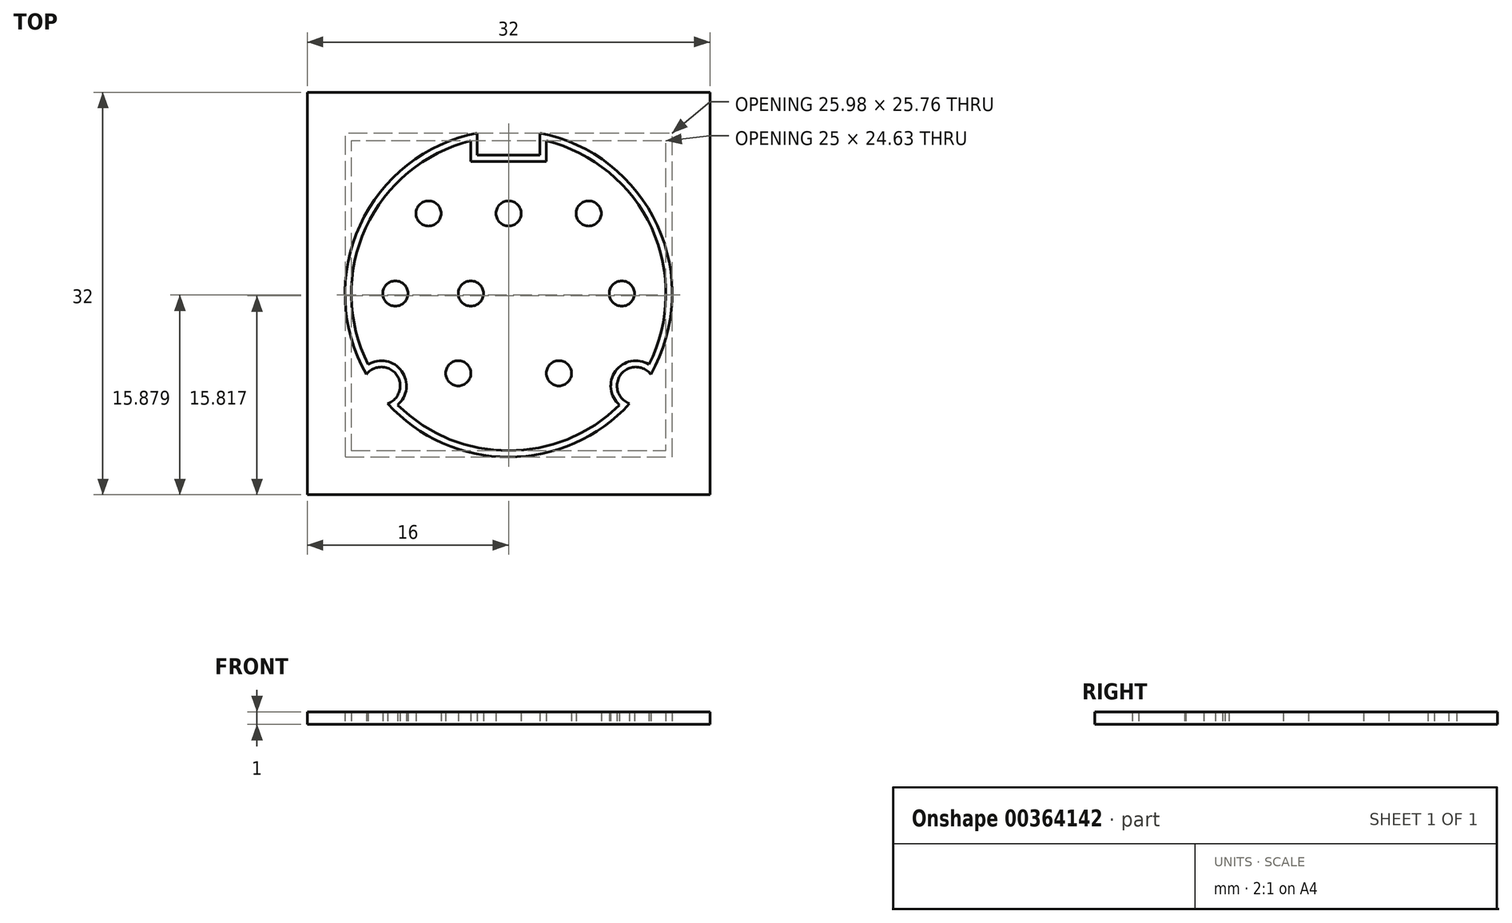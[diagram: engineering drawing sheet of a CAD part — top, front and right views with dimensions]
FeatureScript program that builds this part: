
annotation { "Feature Type Name" : "Feature", "Feature Type Description" : "" }
export const myFeature = defineFeature(function(context is Context, id is Id, definition is map)
    precondition{}
    {
        {
            var Q0;
            Q0=qCreatedBy(makeId("Top.planeOp"),FACE);
            var sketch = newSketch(context, id + "F0", { "sketchPlane" : qUnion([Q0])});
            skArc(sketch, "E0", {"start": v(-12.05, -3.32) * mm, "mid": v(-11.66, -4.5) * mm, "end": v(-11.16, -5.63) * mm});
            skCircle(sketch, "E1", {"center": v(0, 6.36) * mm, "radius": 1 * mm});
            skCircle(sketch, "E2", {"center": v(-9, 0) * mm, "radius": 1 * mm});
            skCircle(sketch, "E3", {"center": v(9, 0) * mm, "radius": 1 * mm});
            skCircle(sketch, "E4", {"center": v(-6.36, 6.36) * mm, "radius": 1 * mm});
            skCircle(sketch, "E5", {"center": v(6.36, 6.36) * mm, "radius": 1 * mm});
            skArc(sketch, "E6", {"start": v(1.5, -12.91) * mm, "mid": v(5.93, -11.57) * mm, "end": v(9.61, -8.75) * mm});
            skLineSegment(sketch, "E7.bottom", {"start": v(16, 16) * mm, "end": v(-16, 16) * mm});
            skLineSegment(sketch, "E7.top", {"start": v(16, -16) * mm, "end": v(-16, -16) * mm});
            skLineSegment(sketch, "E7.left", {"start": v(16, 16) * mm, "end": v(16, -16) * mm});
            skLineSegment(sketch, "E7.right", {"start": v(-16, 16) * mm, "end": v(-16, -16) * mm});
            skArc(sketch, "E8", {"start": v(-3, 12.13) * mm, "mid": v(-11.36, 5.22) * mm, "end": v(-11.16, -5.63) * mm});
            skArc(sketch, "E9", {"start": v(-2.5, 12.76) * mm, "mid": v(-11.81, 5.42) * mm, "end": v(-11.3, -6.42) * mm});
            skCircle(sketch, "E10", {"center": v(-3, 0) * mm, "radius": 1 * mm});
            skCircle(sketch, "E11", {"center": v(-4, -6.34) * mm, "radius": 1 * mm});
            skCircle(sketch, "E12", {"center": v(4, -6.34) * mm, "radius": 1 * mm});
            skLineSegment(sketch, "E13.bottom", {"start": v(2.5, 11) * mm, "end": v(-2.5, 11) * mm});
            skLineSegment(sketch, "E13.left", {"start": v(2.5, 11) * mm, "end": v(2.5, 12.76) * mm});
            skLineSegment(sketch, "E13.right", {"start": v(-2.5, 11) * mm, "end": v(-2.5, 12.76) * mm});
            skLineSegment(sketch, "E14.bottom", {"start": v(3, 10.5) * mm, "end": v(-3, 10.5) * mm});
            skLineSegment(sketch, "E14.left", {"start": v(3, 10.5) * mm, "end": v(3, 12.13) * mm});
            skLineSegment(sketch, "E14.right", {"start": v(-3, 10.5) * mm, "end": v(-3, 12.13) * mm});
            skArc(sketch, "E15", {"start": v(-8.82, -8.86) * mm, "mid": v(-8.5, -6.17) * mm, "end": v(-11.16, -5.63) * mm});
            skArc(sketch, "E16", {"start": v(-9.61, -8.75) * mm, "mid": v(-8.9, -6.46) * mm, "end": v(-11.3, -6.42) * mm});
            skArc(sketch, "E17", {"start": v(11.16, -5.63) * mm, "mid": v(8.5, -6.17) * mm, "end": v(8.82, -8.86) * mm});
            skArc(sketch, "E18", {"start": v(11.3, -6.42) * mm, "mid": v(8.9, -6.46) * mm, "end": v(9.61, -8.75) * mm});
            skArc(sketch, "E19.trimOffspring", {"start": v(-8.82, -8.86) * mm, "mid": v(0, -12.5) * mm, "end": v(8.82, -8.86) * mm});
            skPoint(sketch, "E20.start.orphan", {"position": v(-4, -7.34) * mm});
            skPoint(sketch, "E21.orphan", {"position": v(4, -7.34) * mm});
            skArc(sketch, "E22.trimOffspring", {"start": v(11.16, -5.63) * mm, "mid": v(11.36, 5.22) * mm, "end": v(3, 12.13) * mm});
            skArc(sketch, "E23.trimOffspring", {"start": v(11.16, -5.63) * mm, "mid": v(11.66, -4.5) * mm, "end": v(12.05, -3.32) * mm});
            skArc(sketch, "E24.trimOffspring", {"start": v(-9.61, -8.75) * mm, "mid": v(-5.93, -11.57) * mm, "end": v(-1.5, -12.91) * mm});
            skArc(sketch, "E25.trimOffspring", {"start": v(-9.61, -8.75) * mm, "mid": v(0, -13) * mm, "end": v(9.61, -8.75) * mm});
            skArc(sketch, "E26.trimOffspring", {"start": v(11.3, -6.42) * mm, "mid": v(11.81, 5.42) * mm, "end": v(2.5, 12.76) * mm});
            skSolve(sketch);
        }
        {
            var Q0;
            Q0=makeQuery(id+"F0.imprint","IMPRINT",FACE,{"disambiguationData":[TD([[makeQuery(id+"F0.imprint","IMPRINT",EDGE,{"derivedFrom":sQuery(id+"F0.wireOp",EDGE,"E13.bottom")}),1.0]])]});
            var Q1;
            Q1=makeQuery(id+"F0.imprint","IMPRINT",FACE,{"disambiguationData":[TD([[makeQuery(id+"F0.imprint","IMPRINT",EDGE,{"derivedFrom":sQuery(id+"F0.wireOp",EDGE,"E2")}),1.0]])]});
            var Q2;
            Q2=makeQuery(id+"F0.imprint","IMPRINT",FACE,{"disambiguationData":[TD([[makeQuery(id+"F0.imprint","IMPRINT",EDGE,{"derivedFrom":sQuery(id+"F0.wireOp",EDGE,"E4")}),1.0]])]});
            var Q3;
            Q3=makeQuery(id+"F0.imprint","IMPRINT",FACE,{"disambiguationData":[TD([[makeQuery(id+"F0.imprint","IMPRINT",EDGE,{"derivedFrom":sQuery(id+"F0.wireOp",EDGE,"E1")}),1.0]])]});
            var Q4;
            Q4=makeQuery(id+"F0.imprint","IMPRINT",FACE,{"disambiguationData":[TD([[makeQuery(id+"F0.imprint","IMPRINT",EDGE,{"derivedFrom":sQuery(id+"F0.wireOp",EDGE,"E5")}),1.0]])]});
            var Q5;
            Q5=makeQuery(id+"F0.imprint","IMPRINT",FACE,{"disambiguationData":[TD([[makeQuery(id+"F0.imprint","IMPRINT",EDGE,{"derivedFrom":sQuery(id+"F0.wireOp",EDGE,"E3")}),1.0]])]});
            var Q6;
            Q6=makeQuery(id+"F0.imprint","IMPRINT",FACE,{"disambiguationData":[TD([[makeQuery(id+"F0.imprint","IMPRINT",EDGE,{"derivedFrom":sQuery(id+"F0.wireOp",EDGE,"E10")}),1.0]])]});
            var Q7;
            Q7=makeQuery(id+"F0.imprint","IMPRINT",FACE,{"disambiguationData":[TD([[makeQuery(id+"F0.imprint","IMPRINT",EDGE,{"derivedFrom":sQuery(id+"F0.wireOp",EDGE,"E11")}),1.0]])]});
            var Q8;
            Q8=makeQuery(id+"F0.imprint","IMPRINT",FACE,{"disambiguationData":[TD([[makeQuery(id+"F0.imprint","IMPRINT",EDGE,{"derivedFrom":sQuery(id+"F0.wireOp",EDGE,"E12")}),1.0]])]});
            extrude(context, id + "F1", {"entities" : qUnion([Q0, Q1, Q2, Q3, Q4, Q5, Q6, Q7, Q8]), "depth" : 1 * mm});
        }
        {
            var Q0;
            Q0=makeQuery(id+"F0.imprint","IMPRINT",FACE,{"disambiguationData":[TD([[makeQuery(id+"F0.imprint","IMPRINT",EDGE,{"derivedFrom":sQuery(id+"F0.wireOp",EDGE,"E7.bottom")}),1.0]])]});
            extrude(context, id + "F2", {"entities" : qUnion([Q0]), "depth" : 1 * mm});
        }
    });
